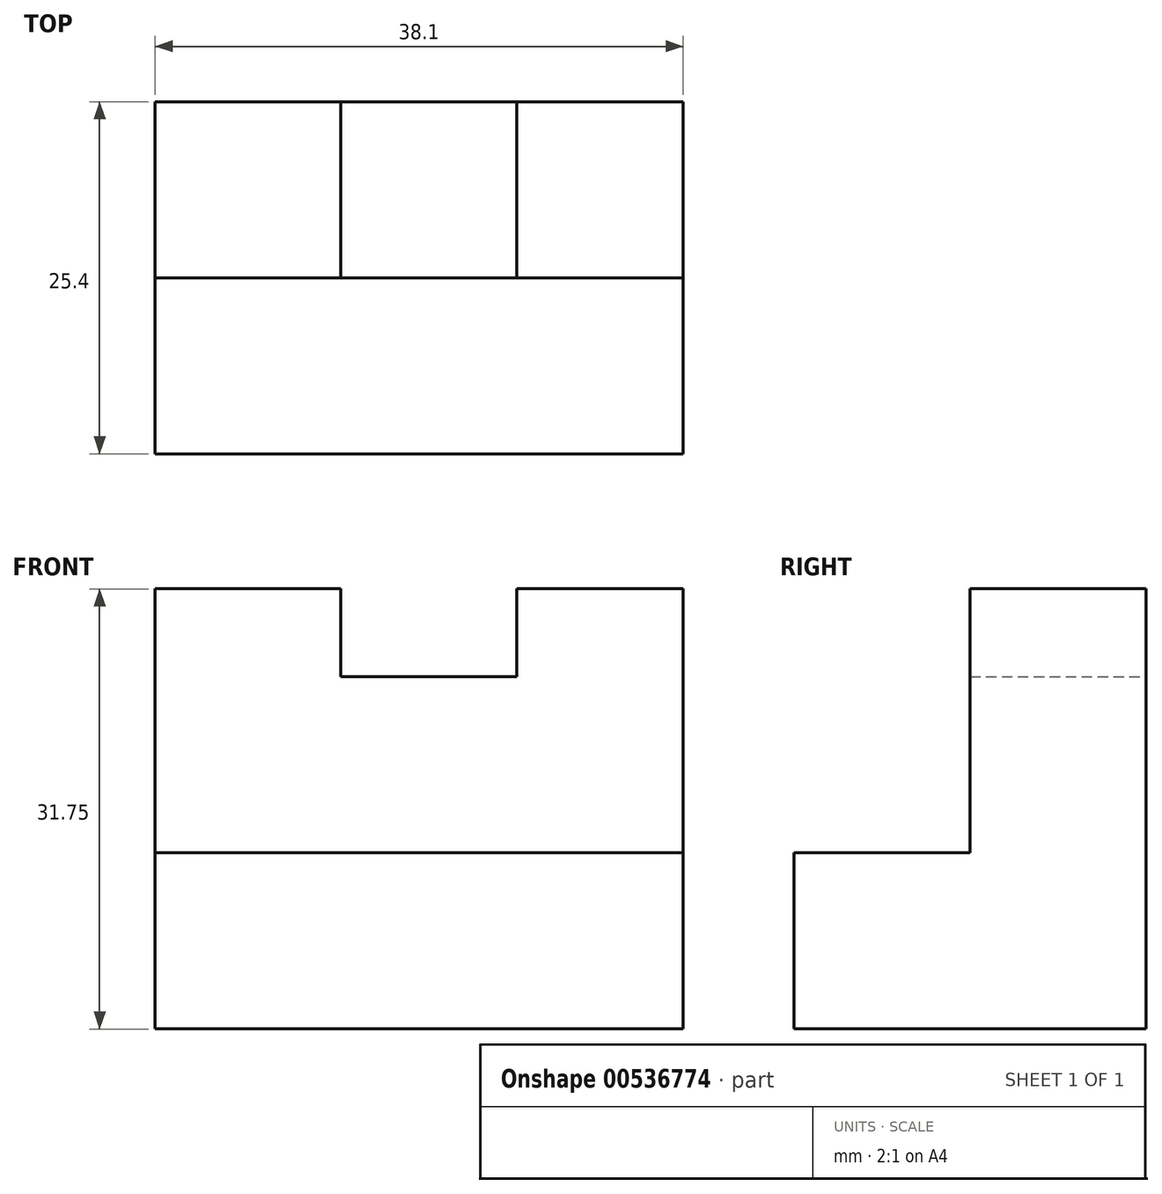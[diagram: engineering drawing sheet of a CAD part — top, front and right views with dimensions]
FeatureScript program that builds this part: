
annotation { "Feature Type Name" : "Feature", "Feature Type Description" : "" }
export const myFeature = defineFeature(function(context is Context, id is Id, definition is map)
    precondition{}
    {
        {
            var Q0;
            Q0=qCreatedBy(makeId("Right.planeOp"),FACE);
            var sketch = newSketch(context, id + "F0", { "sketchPlane" : qUnion([Q0])});
            skLineSegment(sketch, "E0.bottom", {"start": v(-25.4, 9.97) * mm, "end": v(0, 9.97) * mm});
            skLineSegment(sketch, "E0.top", {"start": v(-25.4, -2.73) * mm, "end": v(0, -2.73) * mm});
            skLineSegment(sketch, "E0.left", {"start": v(-25.4, 9.97) * mm, "end": v(-25.4, -2.73) * mm});
            skLineSegment(sketch, "E0.right", {"start": v(0, 9.97) * mm, "end": v(0, -2.73) * mm});
            skLineSegment(sketch, "E1.bottom", {"start": v(-12.7, 9.97) * mm, "end": v(0, 9.97) * mm});
            skLineSegment(sketch, "E1.top", {"start": v(-12.7, 29.02) * mm, "end": v(0, 29.02) * mm});
            skLineSegment(sketch, "E1.left", {"start": v(-12.7, 9.97) * mm, "end": v(-12.7, 29.02) * mm});
            skLineSegment(sketch, "E1.right", {"start": v(0, 9.97) * mm, "end": v(0, 29.02) * mm});
            skSolve(sketch);
        }
        {
            var Q0;
            Q0 = qSketchRegion(id + "F0", true);
            extrude(context, id + "F1", {"entities" : qUnion([Q0]), "depth" : 38.1 * mm, "offsetDistance" : 25.4 * mm});
        }
        {
            var Q0;
            Q0=qCreatedBy(makeId("Front.planeOp"),FACE);
            var sketch = newSketch(context, id + "F2", { "sketchPlane" : qUnion([Q0])});
            skLineSegment(sketch, "E2.bottom", {"start": v(13.39, 29.02) * mm, "end": v(26.09, 29.02) * mm});
            skLineSegment(sketch, "E2.top", {"start": v(13.39, 22.67) * mm, "end": v(26.09, 22.67) * mm});
            skLineSegment(sketch, "E2.left", {"start": v(13.39, 29.02) * mm, "end": v(13.39, 22.67) * mm});
            skLineSegment(sketch, "E2.right", {"start": v(26.09, 29.02) * mm, "end": v(26.09, 22.67) * mm});
            skSolve(sketch);
        }
        {
            var Q0;
            Q0 = qSketchRegion(id + "F2", true);
            extrude(context, id + "F3", {"entities" : qUnion([Q0]), "operationType" : NewBodyOperationType.REMOVE, "depth" : 12.7 * mm, "offsetDistance" : 25.4 * mm});
        }
    });
